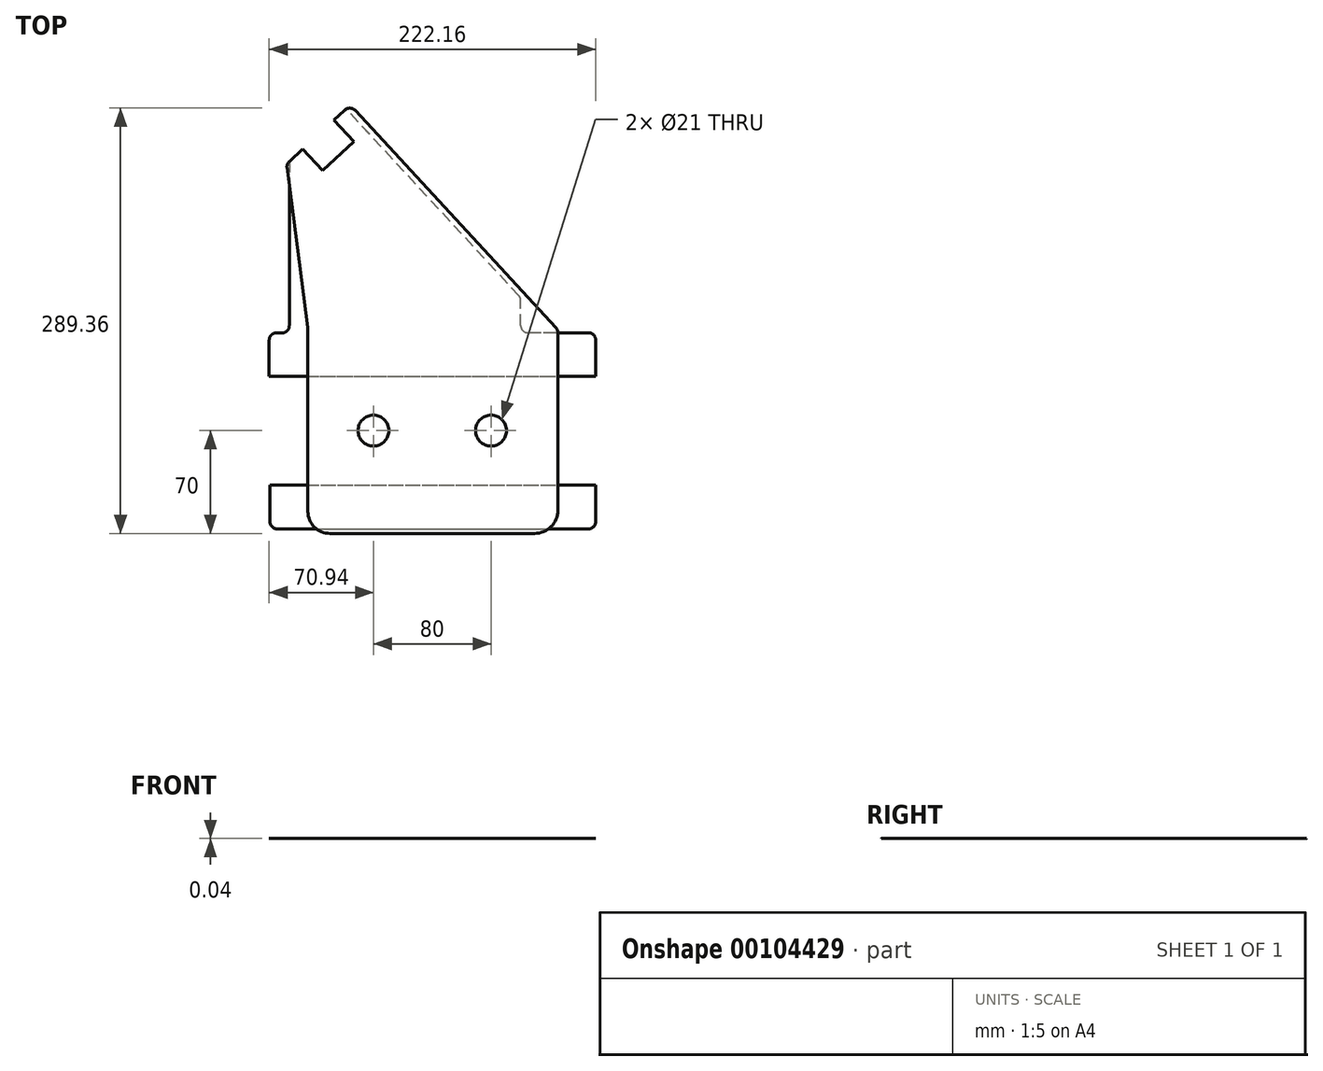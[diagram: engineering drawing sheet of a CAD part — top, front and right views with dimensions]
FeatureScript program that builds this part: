
annotation { "Feature Type Name" : "Feature", "Feature Type Description" : "" }
export const myFeature = defineFeature(function(context is Context, id is Id, definition is map)
    precondition{}
    {
        {
            var Q0;
            Q0=qCreatedBy(makeId("Top.planeOp"),FACE);
            var sketch = newSketch(context, id + "F0", { "sketchPlane" : qUnion([Q0])});
            skCircle(sketch, "E0", {"center": v(-40, 0) * mm, "radius": 10.5 * mm});
            skCircle(sketch, "E1", {"center": v(40, 0) * mm, "radius": 10.5 * mm});
            skLineSegment(sketch, "E2", {"start": v(-40, 0) * mm, "end": v(40, 0) * mm, "construction": true});
            skLineSegment(sketch, "E3", {"start": v(-69.58, -70) * mm, "end": v(69.58, -70) * mm});
            skPoint(sketch, "E4.visualSharp", {"position": v(85.42, -70) * mm});
            skArc(sketch, "E4.filletArc", {"start": v(69.58, -70) * mm, "mid": v(80.78, -65.36) * mm, "end": v(85.42, -54.17) * mm});
            skPoint(sketch, "E5.visualSharp", {"position": v(-84.58, -70) * mm});
            skArc(sketch, "E5.filletArc", {"start": v(-84.58, -55) * mm, "mid": v(-80.2, -65.6) * mm, "end": v(-69.58, -70) * mm});
            skPoint(sketch, "E6.visualSharp", {"position": v(-84.58, 70) * mm});
            skLineSegment(sketch, "E7", {"start": v(0, 120.47) * mm, "end": v(0, -70) * mm, "construction": true});
            skPoint(sketch, "E8", {"position": v(0, -70) * mm});
            skPoint(sketch, "E9", {"position": v(-30, 150) * mm});
            skLineSegment(sketch, "E10", {"start": v(-30, 150) * mm, "end": v(-63.94, 186.71) * mm, "construction": true});
            skLineSegment(sketch, "E11", {"start": v(-74.6, 176.87) * mm, "end": v(-63.94, 186.71) * mm});
            skLineSegment(sketch, "E12", {"start": v(-74.6, 176.87) * mm, "end": v(-88.17, 191.55) * mm});
            skLineSegment(sketch, "E13", {"start": v(-88.17, 191.55) * mm, "end": v(-97.28, 183.13) * mm});
            skLineSegment(sketch, "E14", {"start": v(-98.85, 178.8) * mm, "end": v(-84.63, 70.32) * mm});
            skLineSegment(sketch, "E15.MirrorCS", {"start": v(-53.3, 196.56) * mm, "end": v(-63.94, 186.71) * mm});
            skLineSegment(sketch, "E16.MirrorCS", {"start": v(-53.3, 196.56) * mm, "end": v(-66.87, 211.24) * mm});
            skLineSegment(sketch, "E17.MirrorCS", {"start": v(-66.87, 211.24) * mm, "end": v(-59.53, 218.03) * mm});
            skLineSegment(sketch, "E18", {"start": v(85.42, -54.17) * mm, "end": v(85.42, 66.66) * mm});
            skLineSegment(sketch, "E19", {"start": v(-84.58, -55) * mm, "end": v(-84.58, 69.67) * mm});
            skLineSegment(sketch, "E20", {"start": v(-52.47, 217.75) * mm, "end": v(84.09, 70.06) * mm});
            skPoint(sketch, "E21.visualSharp", {"position": v(85.42, 68.62) * mm});
            skArc(sketch, "E21.filletArc", {"start": v(85.42, 66.66) * mm, "mid": v(85.07, 68.49) * mm, "end": v(84.09, 70.06) * mm});
            skPoint(sketch, "E22.visualSharp", {"position": v(-55.86, 221.42) * mm});
            skArc(sketch, "E22.filletArc", {"start": v(-52.47, 217.75) * mm, "mid": v(-55.94, 219.36) * mm, "end": v(-59.53, 218.03) * mm});
            skPoint(sketch, "E23.visualSharp", {"position": v(-99.18, 181.37) * mm});
            skArc(sketch, "E23.filletArc", {"start": v(-97.28, 183.13) * mm, "mid": v(-98.59, 181.16) * mm, "end": v(-98.85, 178.8) * mm});
            skArc(sketch, "E24.filletArc", {"start": v(-84.58, 69.67) * mm, "mid": v(-84.6, 70) * mm, "end": v(-84.63, 70.32) * mm});
            skSolve(sketch);
        }
        {
            var Q0;
            Q0=makeQuery(id+"F0.imprint","IMPRINT",FACE,{"disambiguationData":[TD([[makeQuery(id+"F0.imprint","IMPRINT",EDGE,{"derivedFrom":sQuery(id+"F0.wireOp",EDGE,"E0")}),-1.0]])]});
            extrude(context, id + "F1", {"entities" : qUnion([Q0]), "offsetDistance" : 25 * mm, "depth" : 9 / 406.4 * mm});
        }
        {
            var Q0;
            Q0=makeQuery(id+"F1.opExtrude","CAP_FACE",FACE,{"disambiguationData":[OSD([sQuery(id+"F0.wireOp",EDGE,"E0"),sQuery(id+"F0.wireOp",EDGE,"E1"),sQuery(id+"F0.wireOp",EDGE,"ORsLJO4S-Lcrg-lpuZ-IpTO-JsHhmnabdJaW"),sQuery(id+"F0.wireOp",EDGE,"E3"),sQuery(id+"F0.wireOp",EDGE,"GkN3tyXG-18Eo-Ar0N-vTS5-nBuOveoUkN9s"),sQuery(id+"F0.wireOp",EDGE,"xwqs8ldE-Amip-0tNx-dzJk-uVIK760CaaNG"),sQuery(id+"F0.wireOp",EDGE,"AQNgvmri-sfpQ-wzMW-YrrT-fI6N64ai6BJn"),sQuery(id+"F0.wireOp",EDGE,"EPBhpeX1-9vd9-T2Hr-ksZR-klpsxm78xYMp"),sQuery(id+"F0.wireOp",EDGE,"4de21265-d169-4b6b-aa7f-9020d00b30fa.filletArc"),sQuery(id+"F0.wireOp",EDGE,"c0dfad71-8511-4710-93e8-2a922c9cec26.filletArc"),sQuery(id+"F0.wireOp",EDGE,"E4.filletArc"),sQuery(id+"F0.wireOp",EDGE,"E5.filletArc"),sQuery(id+"F0.wireOp",EDGE,"E6.filletArc")])],"isStart":true});
            var sketch = newSketch(context, id + "F2", { "sketchPlane" : qUnion([Q0])});
            skArc(sketch, "E25.MirrorCS", {"start": v(106.22, 66.89) * mm, "mid": v(109.76, 65.42) * mm, "end": v(111.22, 61.89) * mm});
            skArc(sketch, "E26.MirrorCS", {"start": v(-110.45, 61.89) * mm, "mid": v(-108.98, 65.42) * mm, "end": v(-105.45, 66.89) * mm});
            skPoint(sketch, "E27.MirrorP", {"position": v(-110.45, 66.89) * mm});
            skPoint(sketch, "E28.MirrorP", {"position": v(111.22, 66.89) * mm});
            skLineSegment(sketch, "E29.MirrorCS", {"start": v(-105.45, 66.89) * mm, "end": v(106.22, 66.89) * mm});
            skLineSegment(sketch, "E30.MirrorCS", {"start": v(-110.45, 37.2) * mm, "end": v(111.22, 37.2) * mm});
            skLineSegment(sketch, "E31.MirrorCS", {"start": v(-110.45, 61.89) * mm, "end": v(-110.45, 37.2) * mm});
            skLineSegment(sketch, "E32.MirrorCS", {"start": v(111.22, 61.89) * mm, "end": v(111.22, 37.2) * mm});
            skSolve(sketch);
        }
        {
            var Q0;
            {var subQ0=sQuery(id+"F2.wireOp",EDGE,"KAC7oBAf-Olne-Nu0Y-fXM1-UTm7T2oT9ZTw.left");Q0=makeQuery(id+"F2.imprint","IMPRINT",FACE,{"disambiguationData":[TD([[makeQuery(id+"F2.imprint","IMPRINT",EDGE,{"derivedFrom":subQ0}),-1.0]])]});}
            var Q1;
            {var subQ5=sQuery(id+"F2.wireOp",EDGE,"KAC7oBAf-Olne-Nu0Y-fXM1-UTm7T2oT9ZTw.bottom");var subQ9=makeQuery(id+"F1.opExtrude","CAP_EDGE",EDGE,{"disambiguationData":[OSD([sQuery(id+"F0.wireOp",EDGE,"E5.filletArc")])],"isStart":false});var subQ11=makeQuery(id+"F2.imprint","INTERSECT",VERTEX,{"derivedFrom":[subQ9,subQ5]});Q1=makeQuery(id+"F2.imprint","IMPRINT",FACE,{"disambiguationData":[TD([[makeQuery(id+"F2.imprint","IMPRINT",EDGE,{"disambiguationData":[TD([[subQ11,-1.0]])],"derivedFrom":subQ5}),1.0]])]});}
            var Q2;
            {var subQ0=sQuery(id+"F2.wireOp",EDGE,"KAC7oBAf-Olne-Nu0Y-fXM1-UTm7T2oT9ZTw.right");Q2=makeQuery(id+"F2.imprint","IMPRINT",FACE,{"disambiguationData":[TD([[makeQuery(id+"F2.imprint","IMPRINT",EDGE,{"derivedFrom":subQ0}),1.0]])]});}
            var Q3;
            {var subQ5=sQuery(id+"F2.wireOp",EDGE,"E25.MirrorCS");Q3=makeQuery(id+"F2.imprint","IMPRINT",FACE,{"disambiguationData":[TD([[makeQuery(id+"F2.imprint","IMPRINT",EDGE,{"derivedFrom":subQ5}),-1.0]])]});}
            var Q4;
            {var subQ0=sQuery(id+"F2.wireOp",EDGE,"E29.MirrorCS");var subQ5=makeQuery(id+"F1.opExtrude","CAP_EDGE",EDGE,{"disambiguationData":[OSD([sQuery(id+"F0.wireOp",EDGE,"E6.filletArc")])],"isStart":false});var subQ9=makeQuery(id+"F2.imprint","INTERSECT",VERTEX,{"derivedFrom":[subQ5,subQ0]});Q4=makeQuery(id+"F2.imprint","IMPRINT",FACE,{"disambiguationData":[TD([[makeQuery(id+"F2.imprint","IMPRINT",EDGE,{"disambiguationData":[TD([[subQ9,-1.0]])],"derivedFrom":subQ0}),-1.0]])]});}
            var Q5;
            {var subQ5=sQuery(id+"F2.wireOp",EDGE,"E26.MirrorCS");Q5=makeQuery(id+"F2.imprint","IMPRINT",FACE,{"disambiguationData":[TD([[makeQuery(id+"F2.imprint","IMPRINT",EDGE,{"derivedFrom":subQ5}),-1.0]])]});}
            extrude(context, id + "F3", {"entities" : qUnion([Q0, Q1, Q2, Q3, Q4, Q5]), "depth" : 9 / 406.4 * mm});
        }
        {
            var Q0;
            Q0=makeQuery(id+"F1.opExtrude","CAP_FACE",FACE,{"disambiguationData":[OSD([sQuery(id+"F0.wireOp",EDGE,"E0"),sQuery(id+"F0.wireOp",EDGE,"E1"),sQuery(id+"F0.wireOp",EDGE,"E3"),sQuery(id+"F0.wireOp",EDGE,"E4.filletArc"),sQuery(id+"F0.wireOp",EDGE,"E5.filletArc"),sQuery(id+"F0.wireOp",EDGE,"E11"),sQuery(id+"F0.wireOp",EDGE,"E12"),sQuery(id+"F0.wireOp",EDGE,"E13"),sQuery(id+"F0.wireOp",EDGE,"E14"),sQuery(id+"F0.wireOp",EDGE,"E15.MirrorCS"),sQuery(id+"F0.wireOp",EDGE,"E16.MirrorCS"),sQuery(id+"F0.wireOp",EDGE,"E17.MirrorCS"),sQuery(id+"F0.wireOp",EDGE,"E18"),sQuery(id+"F0.wireOp",EDGE,"E19"),sQuery(id+"F0.wireOp",EDGE,"E20"),sQuery(id+"F0.wireOp",EDGE,"E21.filletArc"),sQuery(id+"F0.wireOp",EDGE,"E22.filletArc"),sQuery(id+"F0.wireOp",EDGE,"E23.filletArc"),sQuery(id+"F0.wireOp",EDGE,"E24.filletArc")])],"isStart":true});
            var sketch = newSketch(context, id + "F4", { "sketchPlane" : qUnion([Q0])});
            skLineSegment(sketch, "E33", {"start": v(-110.94, -36.8) * mm, "end": v(111.22, -36.8) * mm});
            skLineSegment(sketch, "E34", {"start": v(111.22, -36.8) * mm, "end": v(111.22, -61.5) * mm});
            skLineSegment(sketch, "E35", {"start": v(60.16, -71.5) * mm, "end": v(60.16, -88.4) * mm});
            skLineSegment(sketch, "E36", {"start": v(58.83, -91.8) * mm, "end": v(-58.64, -218.86) * mm});
            skLineSegment(sketch, "E37", {"start": v(-58.64, -218.86) * mm, "end": v(-66.87, -211.24) * mm});
            skLineSegment(sketch, "E38", {"start": v(-66.87, -211.24) * mm, "end": v(-53.3, -196.56) * mm});
            skLineSegment(sketch, "E39", {"start": v(-53.3, -196.56) * mm, "end": v(-74.6, -176.87) * mm});
            skLineSegment(sketch, "E40", {"start": v(-74.6, -176.87) * mm, "end": v(-88.17, -191.55) * mm});
            skLineSegment(sketch, "E41", {"start": v(-88.17, -191.55) * mm, "end": v(-97.28, -183.13) * mm});
            skLineSegment(sketch, "E42", {"start": v(-110.94, -61.5) * mm, "end": v(-110.94, -36.8) * mm});
            skLineSegment(sketch, "E43", {"start": v(-97.28, -183.13) * mm, "end": v(-97.28, -71.39) * mm});
            skLineSegment(sketch, "E44", {"start": v(-102.45, -66.4) * mm, "end": v(-105.78, -66.5) * mm});
            skPoint(sketch, "E45.visualSharp", {"position": v(-110.94, -66.67) * mm});
            skArc(sketch, "E45.filletArc", {"start": v(-110.94, -61.5) * mm, "mid": v(-109.42, -65.1) * mm, "end": v(-105.78, -66.5) * mm});
            skPoint(sketch, "E46.visualSharp", {"position": v(-97.28, -66.22) * mm});
            skArc(sketch, "E46.filletArc", {"start": v(-97.28, -71.39) * mm, "mid": v(-98.8, -67.8) * mm, "end": v(-102.45, -66.4) * mm});
            skPoint(sketch, "E47.visualSharp", {"position": v(60.16, -90.37) * mm});
            skArc(sketch, "E47.filletArc", {"start": v(58.83, -91.8) * mm, "mid": v(59.82, -90.23) * mm, "end": v(60.16, -88.4) * mm});
            skLineSegment(sketch, "E48", {"start": v(106.22, -66.5) * mm, "end": v(65.16, -66.5) * mm});
            skPoint(sketch, "E49.visualSharp", {"position": v(111.22, -66.5) * mm});
            skArc(sketch, "E49.filletArc", {"start": v(106.22, -66.5) * mm, "mid": v(109.76, -65.04) * mm, "end": v(111.22, -61.5) * mm});
            skPoint(sketch, "E50.visualSharp", {"position": v(60.16, -66.5) * mm});
            skArc(sketch, "E50.filletArc", {"start": v(65.16, -66.5) * mm, "mid": v(61.63, -67.97) * mm, "end": v(60.16, -71.5) * mm});
            skSolve(sketch);
        }
        {
            var Q0;
            Q0 = qSketchRegion(id + "F4", true);
            extrude(context, id + "F5", {"entities" : qUnion([Q0]), "operationType" : NewBodyOperationType.ADD, "depth" : 9 / 406.4 * mm, "offsetDistance" : 25 * mm});
        }
    });
